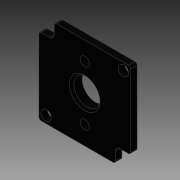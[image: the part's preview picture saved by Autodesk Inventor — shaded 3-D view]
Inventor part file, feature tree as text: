
AUTODESK INVENTOR PART (.ipt)
format: ipt  version: 2014 SP1 (Build 180222100, 222)  size: 257,024 bytes
history: native  units: in
note: dims shown in document units (in); Inventor stores cm internally (conversion verified against a paired STEP export)
features: fillet x1, other x1, imported_body x1
ambient origin geometry x8: Origin, YZ Plane, XZ Plane, XY Plane, X Axis, Y Axis, Z Axis, Center Point
bodies: Body1 (feature_tree)
feature tree (3):
  fillet  "Fillet4"  [1 undecoded]
  other  "217-2822-003 Rev4.ipt1"
  imported_body  "Base1"
note: 1 required parameter value undecoded (feature->parameter linkage not recoverable at this tier; creation-order binding heuristic only, values carry confidence <= 0.55)
